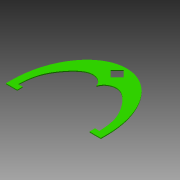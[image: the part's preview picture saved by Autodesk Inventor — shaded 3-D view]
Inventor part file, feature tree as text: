
AUTODESK INVENTOR PART (.ipt)
format: ipt  version: 2015 SP1 (Build 190203100, 203)  size: 126,464 bytes
history: native  units: mm
features: extrude x1
ambient origin geometry x8: Origin, YZ Plane, XZ Plane, XY Plane, X Axis, Y Axis, Z Axis, Center Point
bodies: Solid1 (feature_tree)
feature tree (1):
  extrude  "Extrusion1"  Depth=105.0mm
